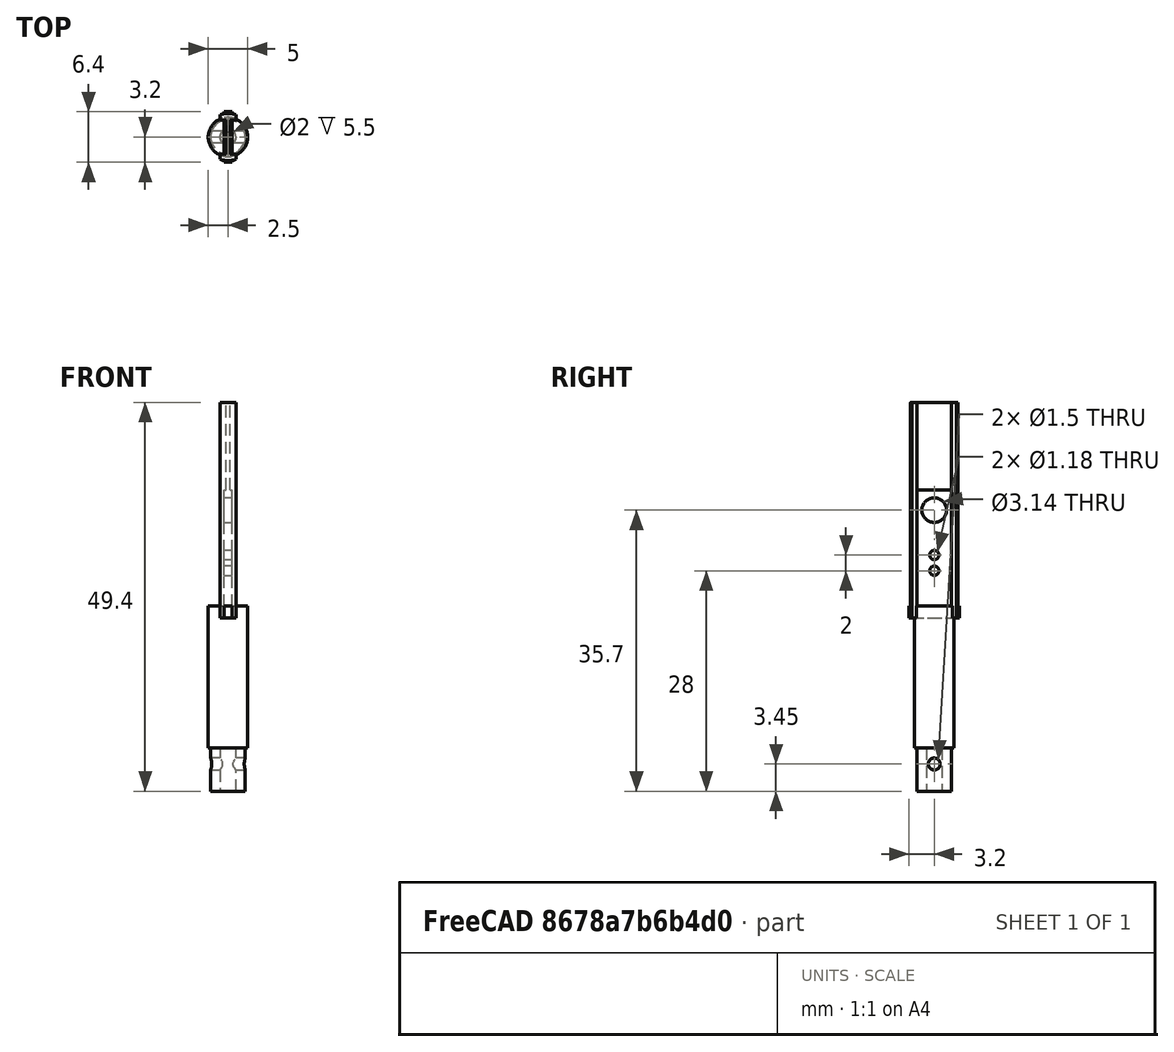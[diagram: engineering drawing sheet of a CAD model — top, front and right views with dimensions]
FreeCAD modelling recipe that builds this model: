
FCSTD DOCUMENT  (FreeCAD 0.20R29603 (Git))
Label: temholder2
License: All rights reserved
LicenseURL: http://en.wikipedia.org/wiki/All_rights_reserved
objects: Part::Cylinder×9, Part::Cut×8, Part::Box×7, Part::MultiFuse×5, Part::MultiCommon×1
note: 30 computed .brp shape members not serialized (recipe doc carries the construction recipe); baked Part::Feature solids carry a one-line shape summary decoded from their .brp

FEATURE [Part::Cylinder] Cylinder  label="Zylinder"
  Angle = 360
  AttacherType = Attacher::AttachEngine3D
  FirstAngle = 0
  Height = 21.5
  Placement = pos=(0,0,-0.5) rot=(0,0,1;0rad)
  Radius = 2.2
  SecondAngle = 0
FEATURE [Part::Cylinder] Cylinder001  label="Zylinder001"
  Angle = 360
  AttacherType = Attacher::AttachEngine3D
  FirstAngle = 0
  Height = 18
  Placement = pos=(0,0,5) rot=(0,0,1;0rad)
  Radius = 2.5
  SecondAngle = 0
FEATURE [Part::Cylinder] Cylinder002  label="Zylinder002"
  Angle = 360
  AttacherType = Attacher::AttachEngine3D
  FirstAngle = 0
  Height = 6.2
  Placement = pos=(-3.25,0,2.95) rot=(0,1,0;1.5708rad)
  Radius = 0.75
  SecondAngle = 0
FEATURE [Part::MultiFuse] Fusion
  Shapes = -> [Cylinder,Cylinder001]
FEATURE [Part::Cut] Cut
  Base = -> Fusion
  Tool = -> Cylinder002
FEATURE [Part::Box] Box  label="Würfel"
  AttacherType = Attacher::AttachEngine3D
  Height = 27.9
  Length = 2
  Placement = pos=(-1,-5,21) rot=(0,0,1;0rad)
  Width = 10
FEATURE [Part::Cylinder] Cylinder003  label="BeamHole"
  Angle = 360
  AttacherType = Attacher::AttachEngine3D
  FirstAngle = 0
  Height = 2
  Placement = pos=(-1,0,35.2) rot=(0,1,0;1.5708rad)
  Radius = 1.1
  SecondAngle = 0
FEATURE [Part::Cylinder] Cylinder004  label="Zylinder004"
  Angle = 360
  AttacherType = Attacher::AttachEngine3D
  FirstAngle = 0
  Height = 27.4
  Placement = pos=(0,0,21.5) rot=(0,0,1;0rad)
  Radius = 3
  SecondAngle = 0
FEATURE [Part::MultiCommon] Common
  Shapes = -> [Cylinder004,Box]
FEATURE [Part::Cut] Cut001
  Base = -> Common
  Tool = -> Cylinder003
FEATURE [Part::Cylinder] Cylinder005  label="Zylinder005"
  Angle = 360
  AttacherType = Attacher::AttachEngine3D
  FirstAngle = 0
  Height = 5.5
  Placement = pos=(0,0,-0.5) rot=(0,0,1;0rad)
  Radius = 1
  SecondAngle = 0
FEATURE [Part::Cut] Cut002
  Base = -> Cut
  Tool = -> Cylinder005
FEATURE [Part::Cylinder] Cylinder006  label="ProbeHole"
  Angle = 360
  AttacherType = Attacher::AttachEngine3D
  FirstAngle = 0
  Height = 20
  Placement = pos=(-4,0,35.2) rot=(0,1,0;1.5708rad)
  Radius = 1.57
  SecondAngle = 0
FEATURE [Part::Cut] Cut003
  Base = -> Cut001
  Tool = -> Cylinder006
FEATURE [Part::Box] Box001  label="Würfel001"
  AttacherType = Attacher::AttachEngine3D
  Height = 27
  Length = 10
  Placement = pos=(1,-2.57,21) rot=(0,0,1;0rad)
  Width = 5.5
FEATURE [Part::Cut] Cut004
  Base = -> Cut003
  Tool = -> Box001
FEATURE [Part::MultiFuse] Fusion001
  Shapes = -> [Cut002,Cut004]
FEATURE [Part::Box] Box002  label="Würfel002"
  AttacherType = Attacher::AttachEngine3D
  Height = 1.5
  Length = 1
  Placement = pos=(-0.5,-3.2,21.5) rot=(0,0,1;0rad)
  Width = 6.4
FEATURE [Part::Box] Box003  label="Würfel003"
  AttacherType = Attacher::AttachEngine3D
  Height = 26
  Length = 10
  Placement = pos=(0.5,-2.19,23) rot=(0,0,1;0rad)
  Width = 4.37
FEATURE [Part::Box] Box004  label="Würfel004"
  AttacherType = Attacher::AttachEngine3D
  Height = 26
  Length = 10
  Placement = pos=(-10.5,-2.19,23) rot=(0,0,1;0rad)
  Width = 4.37
FEATURE [Part::MultiFuse] Fusion002  label="MirrorGrooves"
  Shapes = -> [Box004,Box003]
FEATURE [Part::Cut] Cut005
  Base = -> Fusion001
  Tool = -> Fusion002
FEATURE [Part::Cylinder] Cylinder007  label="M1_6__Thread1"
  Angle = 360
  AttacherType = Attacher::AttachEngine3D
  FirstAngle = 0
  Height = 50
  Placement = pos=(-4,0,29.5) rot=(0,1,0;1.5708rad)
  Radius = 0.59
  SecondAngle = 0
FEATURE [Part::Cylinder] Cylinder008  label="M1_6__Thread2"
  Angle = 360
  AttacherType = Attacher::AttachEngine3D
  FirstAngle = 0
  Height = 50
  Placement = pos=(-4,0,27.5) rot=(0,1,0;1.5708rad)
  Radius = 0.59
  SecondAngle = 0
FEATURE [Part::MultiFuse] Fusion003  label="MirrorMountingHoles"
  Shapes = -> [Cylinder007,Cylinder008]
FEATURE [Part::Cut] Cut006
  Base = -> Cut005
  Tool = -> Fusion003
FEATURE [Part::Box] Box005  label="Würfel005"
  AttacherType = Attacher::AttachEngine3D
  Height = 12
  Length = 10
  Placement = pos=(0.25,-2.19,36.77) rot=(0,0,1;0rad)
  Width = 4.37
FEATURE [Part::Box] Box006  label="Würfel006"
  AttacherType = Attacher::AttachEngine3D
  Height = 12
  Length = 10
  Placement = pos=(-10.25,-2.19,36.77) rot=(0,0,1;0rad)
  Width = 4.37
FEATURE [Part::MultiFuse] Fusion004
  Placement = pos=(0,0,1) rot=(0,0,1;0rad)
  Shapes = -> [Box005,Box006]
FEATURE [Part::Cut] Cut007
  Base = -> Cut006
  Tool = -> Fusion004
